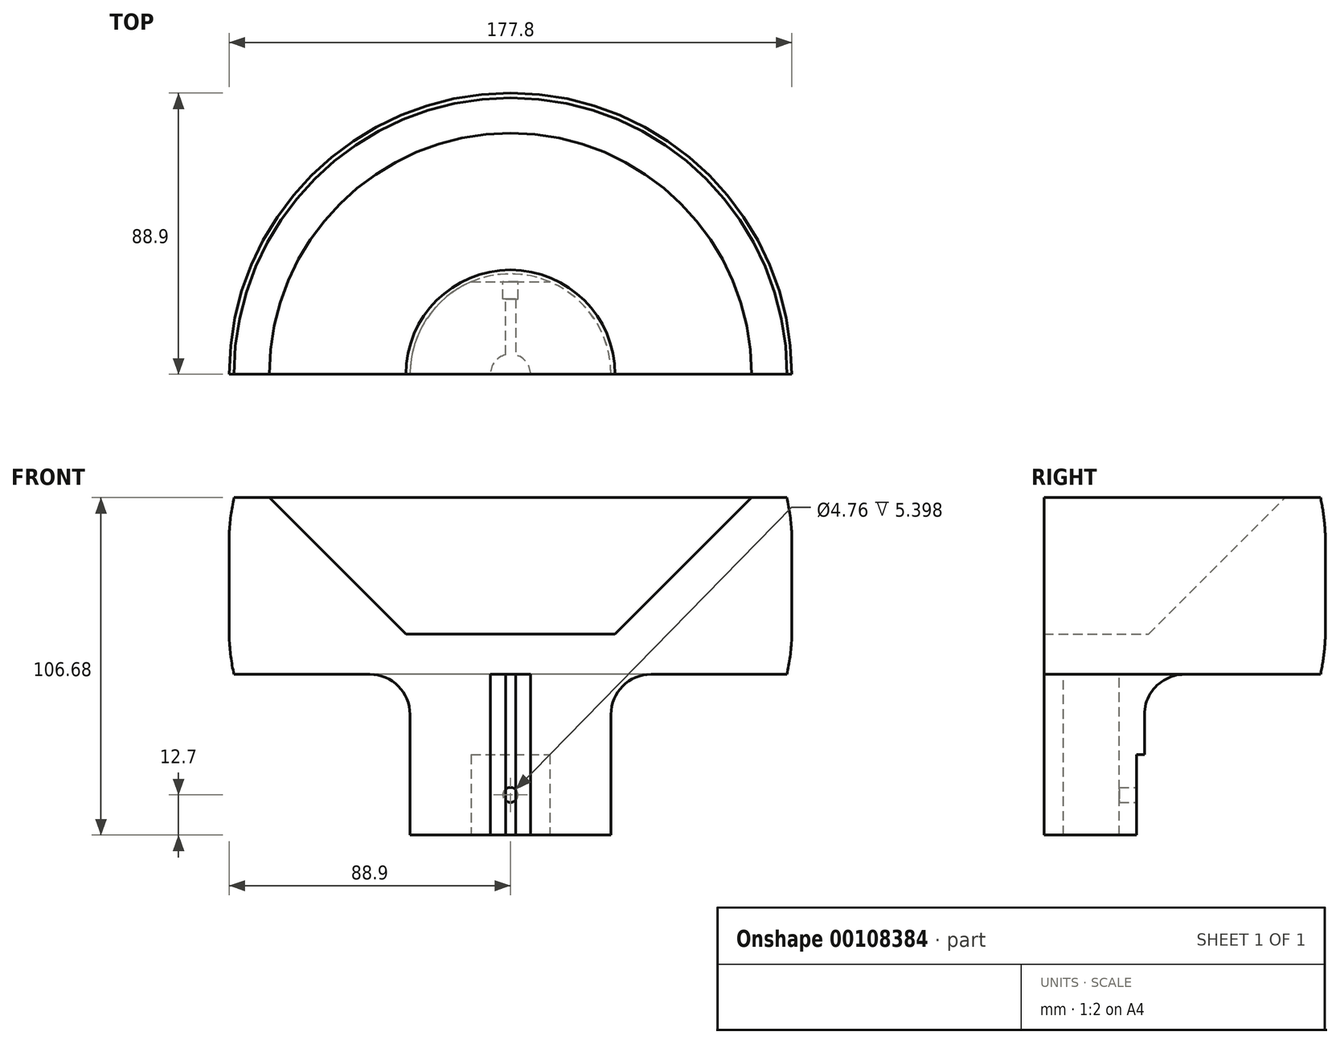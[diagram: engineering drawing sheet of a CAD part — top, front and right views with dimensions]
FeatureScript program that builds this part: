
annotation { "Feature Type Name" : "Feature", "Feature Type Description" : "" }
export const myFeature = defineFeature(function(context is Context, id is Id, definition is map)
    precondition{}
    {
        {
            var Q0;
            Q0=qCreatedBy(makeId("Top.planeOp"),FACE);
            var sketch = newSketch(context, id + "F0", { "sketchPlane" : qUnion([Q0])});
            skCircle(sketch, "E0", {"center": v(0, 0) * mm, "radius": 88.9 * mm});
            skSolve(sketch);
        }
        {
            var Q0;
            Q0=qSketchRegion(id+"F0",true);
            extrude(context, id + "F1", {"entities" : qUnion([Q0]), "depth" : 55.88 * mm});
        }
        {
            var Q0;
            Q0=makeQuery(id+"F1.opExtrude","CAP_FACE",FACE,{"disambiguationData":[OSD([sQuery(id+"F0.wireOp",EDGE,"E0")])],"isStart":false});
            var sketch = newSketch(context, id + "F2", { "sketchPlane" : qUnion([Q0])});
            skCircle(sketch, "E1", {"center": v(0, 0) * mm, "radius": 76.2 * mm});
            skSolve(sketch);
        }
        {
            var Q0;
            Q0=qSketchRegion(id+"F2",true);
            extrude(context, id + "F3", {"entities" : qUnion([Q0]), "operationType" : NewBodyOperationType.REMOVE, "oppositeDirection" : true, "depth" : 43.18 * mm});
        }
        {
            var Q0;
            Q0=makeQuery(id+"F3.boolean.opBoolean","COPY",EDGE,{"derivedFrom":makeQuery(id+"F3.opExtrude","CAP_EDGE",EDGE,{"disambiguationData":[OSD([sQuery(id+"F2.wireOp",EDGE,"E1")])],"isStart":false})});
            chamfer(context, id + "F4", {"entities" : qUnion([Q0]), "width" : 43.18 * mm, "tangentPropagation" : true});
        }
        {
            var Q0;
            Q0=makeQuery(id+"F1.opExtrude","CAP_FACE",FACE,{"disambiguationData":[OSD([sQuery(id+"F0.wireOp",EDGE,"E0")])],"isStart":true});
            var sketch = newSketch(context, id + "F5", { "sketchPlane" : qUnion([Q0])});
            skCircle(sketch, "E2", {"center": v(0, 0) * mm, "radius": 15.88 * mm, "construction": true});
            skArc(sketch, "E3", {"start": v(1.59, -6.15) * mm, "mid": v(0, 6.35) * mm, "end": v(-1.59, -6.15) * mm});
            skCircle(sketch, "E4", {"center": v(0, 0) * mm, "radius": 31.75 * mm});
            skLineSegment(sketch, "E5", {"start": v(0, -6.35) * mm, "end": v(0, -23.81) * mm, "construction": true});
            skLineSegment(sketch, "E6.0", {"start": v(-1.59, -6.35) * mm, "end": v(-1.59, -23.81) * mm});
            skLineSegment(sketch, "E7.0", {"start": v(1.59, -6.35) * mm, "end": v(1.59, -23.81) * mm});
            skLineSegment(sketch, "E8", {"start": v(1.59, -23.81) * mm, "end": v(-1.59, -23.81) * mm});
            skLineSegment(sketch, "E9", {"start": v(1.59, -6.35) * mm, "end": v(1.59, -6.15) * mm});
            skLineSegment(sketch, "E10", {"start": v(-1.59, -6.35) * mm, "end": v(-1.59, -6.15) * mm});
            skSolve(sketch);
        }
        {
            var Q0;
            Q0=makeQuery(id+"F5.imprint","IMPRINT",FACE,{"disambiguationData":[TD([[makeQuery(id+"F5.imprint","IMPRINT",EDGE,{"derivedFrom":sQuery(id+"F5.wireOp",EDGE,"E3")}),-1.0]])]});
            extrude(context, id + "F6", {"entities" : qUnion([Q0]), "operationType" : NewBodyOperationType.ADD, "depth" : 50.8 * mm});
        }
        {
            var Q0;
            Q0=makeQuery(id+"F6.opExtrude","CAP_EDGE",EDGE,{"disambiguationData":[OSD([sQuery(id+"F5.wireOp",EDGE,"E4")])],"isStart":true});
            fillet(context, id + "F7", {"entities" : qUnion([Q0]), "radius" : 12.7 * mm, "tangentPropagation" : true, "allowEdgeOverflow" : false});
        }
        {
            var Q0;
            Q0=makeQuery(id+"F6.opExtrude","CAP_FACE",FACE,{"disambiguationData":[OSD([sQuery(id+"F5.wireOp",EDGE,"E3"),sQuery(id+"F5.wireOp",EDGE,"E4"),sQuery(id+"F5.wireOp",EDGE,"E6.0"),sQuery(id+"F5.wireOp",EDGE,"E7.0"),sQuery(id+"F5.wireOp",EDGE,"E8"),sQuery(id+"F5.wireOp",EDGE,"E9"),sQuery(id+"F5.wireOp",EDGE,"E10")])],"isStart":false});
            var sketch = newSketch(context, id + "F8", { "sketchPlane" : qUnion([Q0])});
            skLineSegment(sketch, "E11", {"start": v(-12.44, -29.21) * mm, "end": v(12.44, -29.21) * mm});
            skSolve(sketch);
        }
        {
            var Q0;
            Q0=qSketchRegion(id+"F8",true);
            var Q1;
            {var subQ0=sQuery(id+"F8.wireOp",EDGE,"E11");Q1=makeQuery(id+"F8.imprint","IMPRINT",FACE,{"disambiguationData":[TD([[makeQuery(id+"F8.imprint","IMPRINT",EDGE,{"derivedFrom":subQ0}),-1.0]])]});}
            extrude(context, id + "F9", {"entities" : qUnion([Q0, Q1]), "operationType" : NewBodyOperationType.REMOVE, "oppositeDirection" : true, "depth" : 25.4 * mm});
        }
        {
            var Q0;
            Q0=makeQuery(id+"F9.boolean.opBoolean","COPY",FACE,{"derivedFrom":makeQuery(id+"F9.opExtrude","SWEPT_FACE",FACE,{"disambiguationData":[OSD([sQuery(id+"F8.wireOp",EDGE,"E11")])]})});
            var sketch = newSketch(context, id + "F10", { "sketchPlane" : qUnion([Q0])});
            skCircle(sketch, "E12", {"center": v(0, -38.1) * mm, "radius": 2.38 * mm});
            skLineSegment(sketch, "E13", {"start": v(-12.44, -38.1) * mm, "end": v(12.44, -38.1) * mm, "construction": true});
            skSolve(sketch);
        }
        {
            var Q0;
            Q0=makeQuery(id+"F10.imprint","IMPRINT",FACE,{"disambiguationData":[TD([[makeQuery(id+"F10.imprint","IMPRINT",EDGE,{"derivedFrom":sQuery(id+"F10.wireOp",EDGE,"E12")}),1.0]])]});
            var Q1;
            Q1=makeQuery(id+"F6.opExtrude","SWEPT_FACE",FACE,{"disambiguationData":[OSD([sQuery(id+"F5.wireOp",EDGE,"E8")])]});
            extrude(context, id + "F11", {"entities" : qUnion([Q0]), "operationType" : NewBodyOperationType.REMOVE, "endBound" : BoundingType.UP_TO_SURFACE, "oppositeDirection" : true, "endBoundEntityFace" : qUnion([Q1]), "depth" : 25.4 * mm});
        }
        {
            var Q0;
            Q0=qCreatedBy(makeId("Right.planeOp"),FACE);
            var sketch = newSketch(context, id + "F12", { "sketchPlane" : qUnion([Q0])});
            skLineSegment(sketch, "E14", {"start": v(88.98, 55.84) * mm, "end": v(88.98, 0) * mm});
            skLineSegment(sketch, "E15.0", {"start": v(87.4, 55.88) * mm, "end": v(87.4, -0.01) * mm});
            skLineSegment(sketch, "E16", {"start": v(87.4, 27.93) * mm, "end": v(88.98, 27.93) * mm});
            skLineSegment(sketch, "E17.0", {"start": v(87.4, 15.23) * mm, "end": v(88.98, 15.23) * mm});
            skLineSegment(sketch, "E18.MirrorCS", {"start": v(87.4, 40.63) * mm, "end": v(88.98, 40.63) * mm});
            skArc(sketch, "E19", {"start": v(88.98, 40.63) * mm, "mid": v(88.6, 48.3) * mm, "end": v(87.4, 55.88) * mm});
            skArc(sketch, "E20.MirrorCS", {"start": v(88.98, 15.23) * mm, "mid": v(88.6, 7.57) * mm, "end": v(87.4, -0.01) * mm});
            skLineSegment(sketch, "E21", {"start": v(88.98, 0) * mm, "end": v(87.4, -0.01) * mm});
            skLineSegment(sketch, "E22", {"start": v(88.98, 55.84) * mm, "end": v(88.98, 55.98) * mm});
            skLineSegment(sketch, "E23", {"start": v(88.98, 55.98) * mm, "end": v(87.4, 55.88) * mm});
            skSolve(sketch);
        }
        {
            var Q0;
            {var subQ0=sQuery(id+"F12.wireOp",EDGE,"E21");Q0=makeQuery(id+"F12.imprint","IMPRINT",FACE,{"disambiguationData":[TD([[makeQuery(id+"F12.imprint","IMPRINT",EDGE,{"derivedFrom":subQ0}),-1.0]])]});}
            var Q1;
            {var subQ0=sQuery(id+"F12.wireOp",EDGE,"8GxrKduf-Hcsh-5AT2-bgIt-kJHD9TFqB5aX");Q1=makeQuery(id+"F12.imprint","IMPRINT",FACE,{"disambiguationData":[TD([[makeQuery(id+"F12.imprint","IMPRINT",EDGE,{"derivedFrom":subQ0}),-1.0]])]});}
            var Q2;
            {var subQ0=sQuery(id+"F12.wireOp",EDGE,"E22");Q2=makeQuery(id+"F12.imprint","IMPRINT",FACE,{"disambiguationData":[TD([[makeQuery(id+"F12.imprint","IMPRINT",EDGE,{"derivedFrom":subQ0}),1.0]])]});}
            var Q3;
            Q3=makeQuery(id+"F1.opExtrude","CAP_EDGE",EDGE,{"disambiguationData":[OSD([sQuery(id+"F0.wireOp",EDGE,"E0")])],"isStart":true});
            revolve(context, id + "F13", {"operationType" : NewBodyOperationType.REMOVE, "entities" : qUnion([Q0, Q1, Q2]), "axis" : qUnion([Q3]), "revolveType" : RevolveType.FULL, "oppositeDirection" : true});
        }
        {
            var Q0;
            Q0=makeQuery(id+"F13.boolean.opBoolean","INTERSECT",EDGE,{"derivedFrom":[makeQuery(id+"F1.opExtrude","SWEPT_FACE",FACE,{"disambiguationData":[OSD([sQuery(id+"F0.wireOp",EDGE,"E0")])]}),makeQuery(id+"F13.opRevolve","SWEPT_FACE",FACE,{"disambiguationData":[OSD([sQuery(id+"F12.wireOp",EDGE,"E20.MirrorCS")])]})]});
            var Q1;
            Q1=makeQuery(id+"F13.boolean.opBoolean","INTERSECT",EDGE,{"derivedFrom":[makeQuery(id+"F1.opExtrude","SWEPT_FACE",FACE,{"disambiguationData":[OSD([sQuery(id+"F0.wireOp",EDGE,"E0")])]}),makeQuery(id+"F13.opRevolve","SWEPT_FACE",FACE,{"disambiguationData":[OSD([sQuery(id+"F12.wireOp",EDGE,"E19")])]})]});
            fillet(context, id + "F14", {"entities" : qUnion([Q0, Q1]), "radius" : 5.08 * mm, "tangentPropagation" : true, "allowEdgeOverflow" : false});
        }
        {
            var Q0;
            Q0=makeQuery(id+"F6.opExtrude","CAP_FACE",FACE,{"disambiguationData":[OSD([sQuery(id+"F5.wireOp",EDGE,"E3"),sQuery(id+"F5.wireOp",EDGE,"E4"),sQuery(id+"F5.wireOp",EDGE,"E6.0"),sQuery(id+"F5.wireOp",EDGE,"E7.0"),sQuery(id+"F5.wireOp",EDGE,"E8"),sQuery(id+"F5.wireOp",EDGE,"E9"),sQuery(id+"F5.wireOp",EDGE,"E10")])],"isStart":false});
            var sketch = newSketch(context, id + "F15", { "sketchPlane" : qUnion([Q0])});
            skLineSegment(sketch, "E24.bottom", {"start": v(108.67, 0) * mm, "end": v(-105.76, 0) * mm});
            skLineSegment(sketch, "E24.top", {"start": v(108.67, 106.87) * mm, "end": v(-105.76, 106.87) * mm});
            skLineSegment(sketch, "E24.left", {"start": v(108.67, 0) * mm, "end": v(108.67, 106.87) * mm});
            skLineSegment(sketch, "E24.right", {"start": v(-105.76, 0) * mm, "end": v(-105.76, 106.87) * mm});
            skSolve(sketch);
        }
        {
            var Q0;
            Q0 = qSketchRegion(id + "F15", true);
            extrude(context, id + "F16", {"entities" : qUnion([Q0]), "operationType" : NewBodyOperationType.REMOVE, "oppositeDirection" : true, "depth" : 165.96 * mm});
        }
    });
